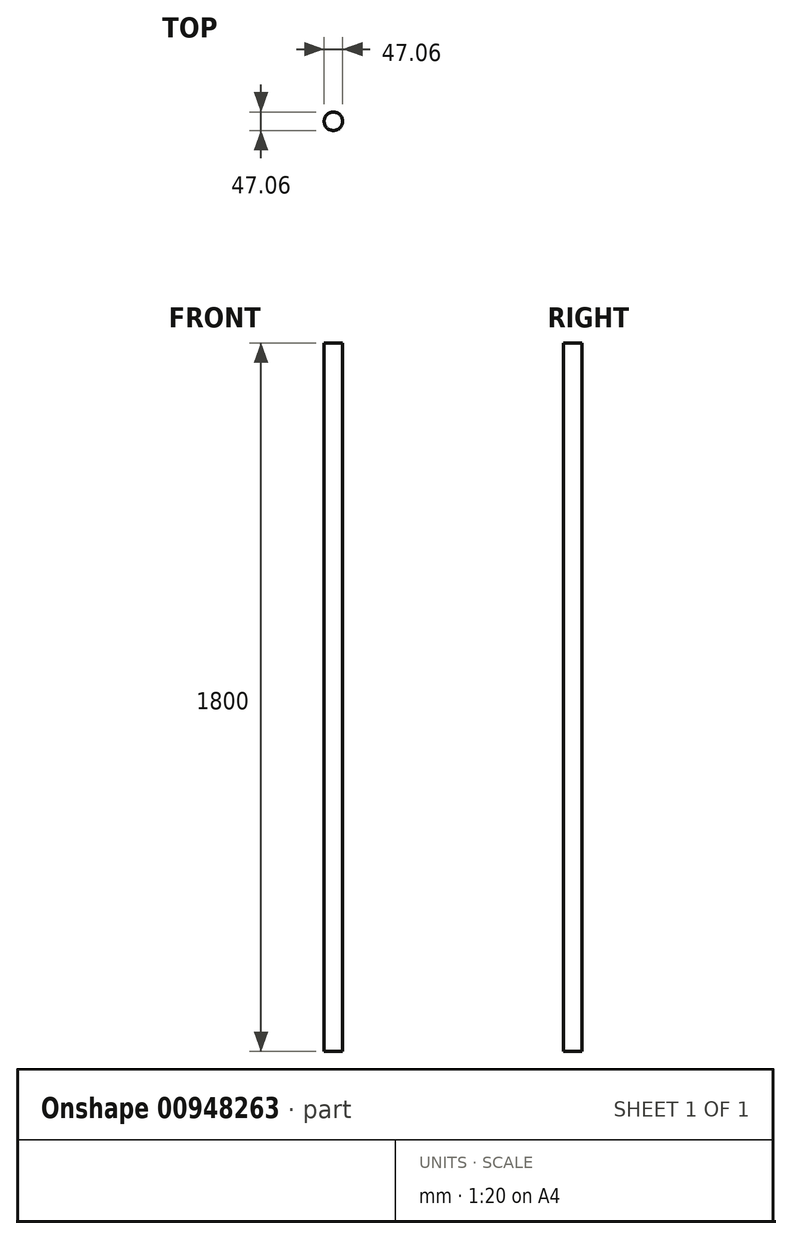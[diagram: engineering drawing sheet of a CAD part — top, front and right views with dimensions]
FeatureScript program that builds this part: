
annotation { "Feature Type Name" : "Feature", "Feature Type Description" : "" }
export const myFeature = defineFeature(function(context is Context, id is Id, definition is map)
    precondition{}
    {
        {
            var Q0;
            Q0=qCreatedBy(makeId("Top.planeOp"),FACE);
            var sketch = newSketch(context, id + "F0", { "sketchPlane" : qUnion([Q0])});
            skCircle(sketch, "E0", {"center": v(0, 0) * mm, "radius": 23.53 * mm});
            skSolve(sketch);
        }
        {
            var Q0;
            Q0=makeQuery(id+"F0.imprint","IMPRINT",FACE,{"disambiguationData":[TD([[makeQuery(id+"F0.imprint","IMPRINT",EDGE,{"derivedFrom":sQuery(id+"F0.wireOp",EDGE,"E0")}),1.0]])]});
            extrude(context, id + "F1", {"entities" : qUnion([Q0]), "depth" : 1800 * mm, "offsetDistance" : 25 * mm});
        }
    });
